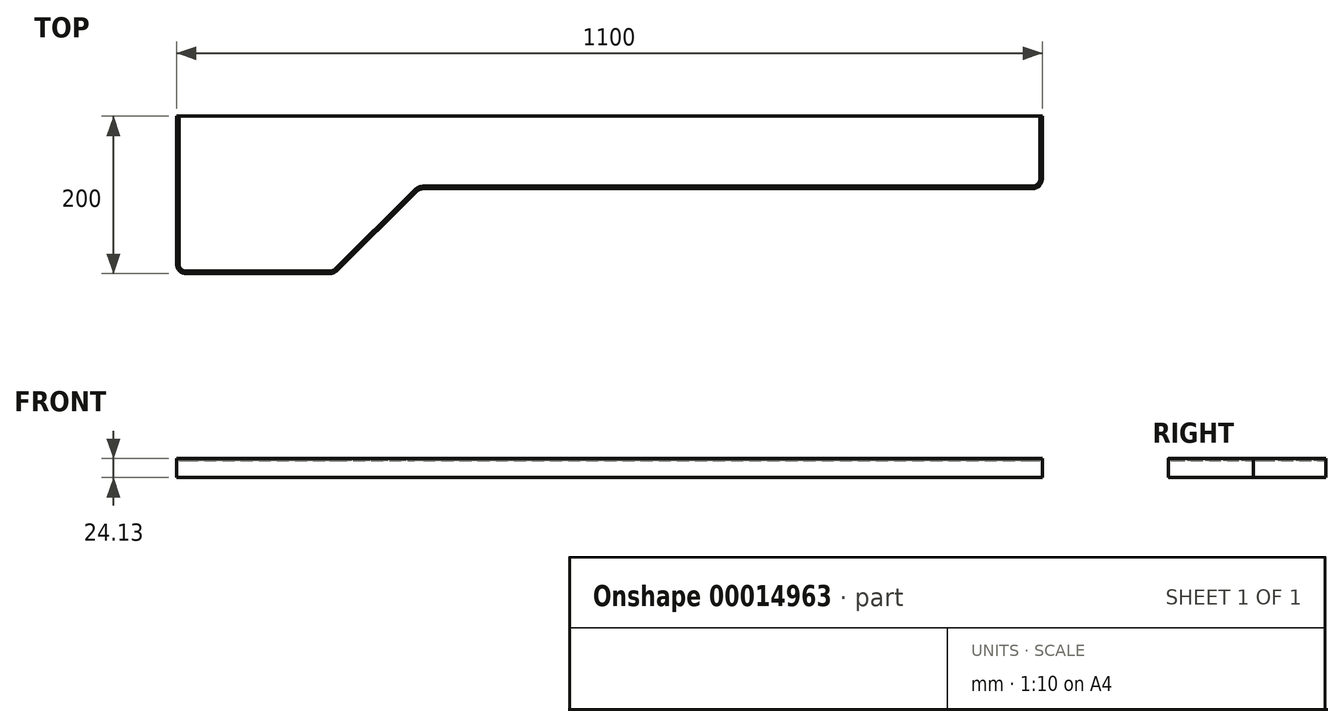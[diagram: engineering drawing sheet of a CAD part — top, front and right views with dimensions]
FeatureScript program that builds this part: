
annotation { "Feature Type Name" : "Feature", "Feature Type Description" : "" }
export const myFeature = defineFeature(function(context is Context, id is Id, definition is map)
    precondition{}
    {
        {
            var Q0;
            Q0=qCreatedBy(makeId("Top.planeOp"),FACE);
            var sketch = newSketch(context, id + "F0", { "sketchPlane" : qUnion([Q0])});
            skLineSegment(sketch, "E0", {"start": v(-406.3, 0) * mm, "end": v(-406.3, -187.3) * mm});
            skLineSegment(sketch, "E1", {"start": v(-393.6, -200) * mm, "end": v(-211.53, -200) * mm});
            skLineSegment(sketch, "E2", {"start": v(-202.58, -196.3) * mm, "end": v(-101.4, -95.77) * mm});
            skLineSegment(sketch, "E3", {"start": v(-92.45, -92.08) * mm, "end": v(681, -92.08) * mm});
            skLineSegment(sketch, "E4", {"start": v(693.7, -79.38) * mm, "end": v(693.7, 0) * mm});
            skLineSegment(sketch, "E5", {"start": v(693.7, 0) * mm, "end": v(690.53, 0) * mm});
            skPoint(sketch, "E6.visualSharp", {"position": v(-406.3, -200) * mm});
            skArc(sketch, "E6.filletArc", {"start": v(-406.3, -187.3) * mm, "mid": v(-402.57, -196.28) * mm, "end": v(-393.6, -200) * mm});
            skPoint(sketch, "E7.visualSharp", {"position": v(-97.69, -92.08) * mm});
            skArc(sketch, "E7.filletArc", {"start": v(-92.45, -92.08) * mm, "mid": v(-97.3, -93.03) * mm, "end": v(-101.4, -95.77) * mm});
            skPoint(sketch, "E8.visualSharp", {"position": v(-206.3, -200) * mm});
            skArc(sketch, "E8.filletArc", {"start": v(-211.53, -200) * mm, "mid": v(-206.69, -199.04) * mm, "end": v(-202.58, -196.3) * mm});
            skPoint(sketch, "E9.visualSharp", {"position": v(693.7, -92.08) * mm});
            skArc(sketch, "E9.filletArc", {"start": v(681, -92.08) * mm, "mid": v(689.99, -88.36) * mm, "end": v(693.7, -79.38) * mm});
            skLineSegment(sketch, "E10.0", {"start": v(690.53, -79.37) * mm, "end": v(690.53, 0) * mm});
            skArc(sketch, "E10.1", {"start": v(681, -88.9) * mm, "mid": v(687.74, -86.11) * mm, "end": v(690.53, -79.37) * mm});
            skLineSegment(sketch, "E10.2", {"start": v(-92.45, -88.9) * mm, "end": v(681, -88.9) * mm});
            skArc(sketch, "E10.3", {"start": v(-92.45, -88.9) * mm, "mid": v(-98.5, -90.1) * mm, "end": v(-103.64, -93.51) * mm});
            skLineSegment(sketch, "E10.4", {"start": v(-204.81, -194.06) * mm, "end": v(-103.64, -93.51) * mm});
            skArc(sketch, "E10.5", {"start": v(-211.53, -196.83) * mm, "mid": v(-207.9, -196.1) * mm, "end": v(-204.81, -194.06) * mm});
            skLineSegment(sketch, "E10.6", {"start": v(-393.6, -196.83) * mm, "end": v(-211.53, -196.83) * mm});
            skArc(sketch, "E10.7", {"start": v(-403.12, -187.3) * mm, "mid": v(-400.33, -194.04) * mm, "end": v(-393.6, -196.83) * mm});
            skLineSegment(sketch, "E10.8", {"start": v(-403.12, 0) * mm, "end": v(-403.12, 0) * mm});
            skLineSegment(sketch, "E11", {"start": v(-403.12, 0) * mm, "end": v(-403.12, -187.3) * mm});
            skLineSegment(sketch, "E12", {"start": v(-403.12, 0) * mm, "end": v(-406.3, 0) * mm});
            skLineSegment(sketch, "E13", {"start": v(690.53, 0) * mm, "end": v(-403.12, 0) * mm});
            skSolve(sketch);
        }
        {
            var Q0;
            Q0=makeQuery(id+"F0.imprint","IMPRINT",FACE,{"disambiguationData":[TD([[makeQuery(id+"F0.imprint","IMPRINT",EDGE,{"derivedFrom":sQuery(id+"F0.wireOp",EDGE,"E10.0")}),1.0]])]});
            var Q1;
            Q1=makeQuery(id+"F0.imprint","IMPRINT",FACE,{"disambiguationData":[TD([[makeQuery(id+"F0.imprint","IMPRINT",EDGE,{"derivedFrom":sQuery(id+"F0.wireOp",EDGE,"E0")}),1.0]])]});
            extrude(context, id + "F1", {"entities" : qUnion([Q0, Q1]), "oppositeDirection" : true, "depth" : 24.13 * mm});
        }
        {
            var Q0;
            Q0=makeQuery(id+"F0.imprint","IMPRINT",FACE,{"disambiguationData":[TD([[makeQuery(id+"F0.imprint","IMPRINT",EDGE,{"derivedFrom":sQuery(id+"F0.wireOp",EDGE,"E10.0")}),1.0]])]});
            extrude(context, id + "F2", {"entities" : qUnion([Q0]), "oppositeDirection" : true, "depth" : 2.54 * mm});
        }
        {
            var Q0;
            Q0=makeQuery(id+"F2.opExtrude","SWEPT_BODY",BODY,{"disambiguationData":[OSD([sQuery(id+"F0.wireOp",EDGE,"E10.0"),sQuery(id+"F0.wireOp",EDGE,"E10.1"),sQuery(id+"F0.wireOp",EDGE,"E10.2"),sQuery(id+"F0.wireOp",EDGE,"E10.3"),sQuery(id+"F0.wireOp",EDGE,"E10.4"),sQuery(id+"F0.wireOp",EDGE,"E10.5"),sQuery(id+"F0.wireOp",EDGE,"E10.6"),sQuery(id+"F0.wireOp",EDGE,"E10.7"),sQuery(id+"F0.wireOp",EDGE,"E11"),sQuery(id+"F0.wireOp",EDGE,"E13")])]});
            var Q1;
            Q1=makeQuery(id+"F1.opExtrude","SWEPT_BODY",BODY,{"disambiguationData":[OSD([sQuery(id+"F0.wireOp",EDGE,"E0"),sQuery(id+"F0.wireOp",EDGE,"E1"),sQuery(id+"F0.wireOp",EDGE,"E2"),sQuery(id+"F0.wireOp",EDGE,"E3"),sQuery(id+"F0.wireOp",EDGE,"E4"),sQuery(id+"F0.wireOp",EDGE,"E5"),sQuery(id+"F0.wireOp",EDGE,"E6.filletArc"),sQuery(id+"F0.wireOp",EDGE,"E7.filletArc"),sQuery(id+"F0.wireOp",EDGE,"E8.filletArc"),sQuery(id+"F0.wireOp",EDGE,"E9.filletArc"),sQuery(id+"F0.wireOp",EDGE,"E12"),sQuery(id+"F0.wireOp",EDGE,"E13")])]});
            booleanBodies(context, id + "F3", {"operationType" : BooleanOperationType.SUBTRACTION, "tools" : qUnion([Q0]), "targets" : qUnion([Q1])});
        }
    });
